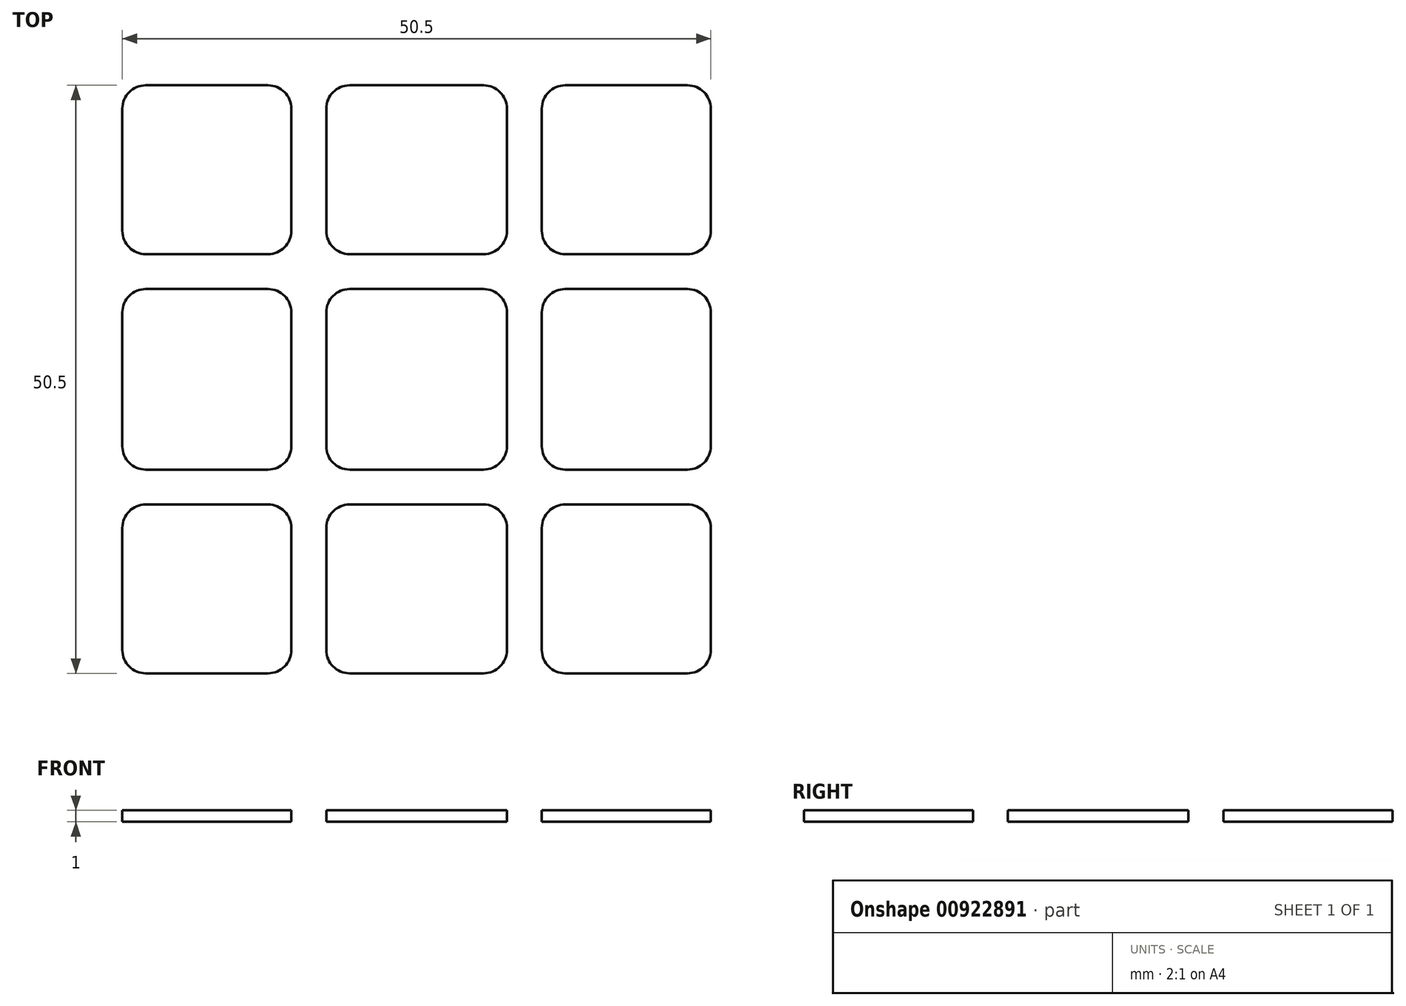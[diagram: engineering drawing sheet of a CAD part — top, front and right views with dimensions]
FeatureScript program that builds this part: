
annotation { "Feature Type Name" : "Feature", "Feature Type Description" : "" }
export const myFeature = defineFeature(function(context is Context, id is Id, definition is map)
    precondition{}
    {
        {
            var Q0;
            Q0=qCreatedBy(makeId("Top.planeOp"),FACE);
            var sketch = newSketch(context, id + "F0", { "sketchPlane" : qUnion([Q0])});
            skLineSegment(sketch, "E0.bottom", {"start": v(27.75, 27.75) * mm, "end": v(-27.75, 27.75) * mm, "construction": true});
            skLineSegment(sketch, "E0.top", {"start": v(27.75, -27.75) * mm, "end": v(-27.75, -27.75) * mm, "construction": true});
            skLineSegment(sketch, "E0.left", {"start": v(27.75, 27.75) * mm, "end": v(27.75, -27.75) * mm, "construction": true});
            skLineSegment(sketch, "E0.right", {"start": v(-27.75, 27.75) * mm, "end": v(-27.75, -27.75) * mm, "construction": true});
            skPoint(sketch, "E0.middle", {"position": v(0, 0) * mm});
            skLineSegment(sketch, "E1", {"start": v(-9.25, 27.75) * mm, "end": v(-9.25, -27.75) * mm, "construction": true});
            skLineSegment(sketch, "E2.1.0", {"start": v(-27.75, -9.25) * mm, "end": v(27.75, -9.25) * mm, "construction": true});
            skLineSegment(sketch, "E2.2.0", {"start": v(9.25, -27.75) * mm, "end": v(9.25, 27.75) * mm, "construction": true});
            skLineSegment(sketch, "E2.3.0", {"start": v(27.75, 9.25) * mm, "end": v(-27.75, 9.25) * mm, "construction": true});
            skLineSegment(sketch, "E3.bottom", {"start": v(-23.25, -10.75) * mm, "end": v(-12.75, -10.75) * mm});
            skLineSegment(sketch, "E3.top", {"start": v(-23.25, -25.25) * mm, "end": v(-12.75, -25.25) * mm});
            skLineSegment(sketch, "E3.left", {"start": v(-25.25, -12.75) * mm, "end": v(-25.25, -23.25) * mm});
            skLineSegment(sketch, "E3.right", {"start": v(-10.75, -12.75) * mm, "end": v(-10.75, -23.25) * mm});
            skLineSegment(sketch, "E4.bottom", {"start": v(-5.75, -10.75) * mm, "end": v(5.75, -10.75) * mm});
            skLineSegment(sketch, "E4.top", {"start": v(-5.75, -25.25) * mm, "end": v(5.75, -25.25) * mm});
            skLineSegment(sketch, "E4.left", {"start": v(-7.75, -12.75) * mm, "end": v(-7.75, -23.25) * mm});
            skLineSegment(sketch, "E4.right", {"start": v(7.75, -12.75) * mm, "end": v(7.75, -23.25) * mm});
            skLineSegment(sketch, "E5.bottom", {"start": v(5.75, 7.75) * mm, "end": v(-5.75, 7.75) * mm});
            skLineSegment(sketch, "E5.top", {"start": v(5.75, -7.75) * mm, "end": v(-5.75, -7.75) * mm});
            skLineSegment(sketch, "E5.left", {"start": v(7.75, 5.75) * mm, "end": v(7.75, -5.75) * mm});
            skLineSegment(sketch, "E5.right", {"start": v(-7.75, 5.75) * mm, "end": v(-7.75, -5.75) * mm});
            skPoint(sketch, "E6.visualSharp", {"position": v(-25.25, -10.75) * mm});
            skArc(sketch, "E6.filletArc", {"start": v(-23.25, -10.75) * mm, "mid": v(-24.66, -11.34) * mm, "end": v(-25.25, -12.75) * mm});
            skPoint(sketch, "E7.visualSharp", {"position": v(-25.25, -25.25) * mm});
            skArc(sketch, "E7.filletArc", {"start": v(-25.25, -23.25) * mm, "mid": v(-24.66, -24.66) * mm, "end": v(-23.25, -25.25) * mm});
            skPoint(sketch, "E8.visualSharp", {"position": v(-10.75, -25.25) * mm});
            skArc(sketch, "E8.filletArc", {"start": v(-12.75, -25.25) * mm, "mid": v(-11.34, -24.66) * mm, "end": v(-10.75, -23.25) * mm});
            skPoint(sketch, "E9.visualSharp", {"position": v(-10.75, -10.75) * mm});
            skArc(sketch, "E9.filletArc", {"start": v(-10.75, -12.75) * mm, "mid": v(-11.34, -11.34) * mm, "end": v(-12.75, -10.75) * mm});
            skPoint(sketch, "E10.visualSharp", {"position": v(-7.75, -10.75) * mm});
            skArc(sketch, "E10.filletArc", {"start": v(-5.75, -10.75) * mm, "mid": v(-7.16, -11.34) * mm, "end": v(-7.75, -12.75) * mm});
            skPoint(sketch, "E11.visualSharp", {"position": v(-7.75, -25.25) * mm});
            skArc(sketch, "E11.filletArc", {"start": v(-7.75, -23.25) * mm, "mid": v(-7.16, -24.66) * mm, "end": v(-5.75, -25.25) * mm});
            skPoint(sketch, "E12.visualSharp", {"position": v(7.75, -25.25) * mm});
            skArc(sketch, "E12.filletArc", {"start": v(5.75, -25.25) * mm, "mid": v(7.16, -24.66) * mm, "end": v(7.75, -23.25) * mm});
            skPoint(sketch, "E13.visualSharp", {"position": v(7.75, -10.75) * mm});
            skArc(sketch, "E13.filletArc", {"start": v(7.75, -12.75) * mm, "mid": v(7.16, -11.34) * mm, "end": v(5.75, -10.75) * mm});
            skPoint(sketch, "E14.visualSharp", {"position": v(7.75, -7.75) * mm});
            skArc(sketch, "E14.filletArc", {"start": v(5.75, -7.75) * mm, "mid": v(7.16, -7.16) * mm, "end": v(7.75, -5.75) * mm});
            skPoint(sketch, "E15.visualSharp", {"position": v(7.75, 7.75) * mm});
            skArc(sketch, "E15.filletArc", {"start": v(7.75, 5.75) * mm, "mid": v(7.16, 7.16) * mm, "end": v(5.75, 7.75) * mm});
            skPoint(sketch, "E16.visualSharp", {"position": v(-7.75, 7.75) * mm});
            skArc(sketch, "E16.filletArc", {"start": v(-5.75, 7.75) * mm, "mid": v(-7.16, 7.16) * mm, "end": v(-7.75, 5.75) * mm});
            skPoint(sketch, "E17.visualSharp", {"position": v(-7.75, -7.75) * mm});
            skArc(sketch, "E17.filletArc", {"start": v(-7.75, -5.75) * mm, "mid": v(-7.16, -7.16) * mm, "end": v(-5.75, -7.75) * mm});
            skLineSegment(sketch, "E18.1.0", {"start": v(10.75, -5.75) * mm, "end": v(10.75, 5.75) * mm});
            skPoint(sketch, "E18.1.1", {"position": v(10.75, -7.75) * mm});
            skPoint(sketch, "E18.1.2", {"position": v(25.25, -7.75) * mm});
            skLineSegment(sketch, "E18.1.3", {"start": v(25.25, -5.75) * mm, "end": v(25.25, 5.75) * mm});
            skPoint(sketch, "E18.1.4", {"position": v(10.75, -10.75) * mm});
            skLineSegment(sketch, "E18.1.5", {"start": v(12.75, -25.25) * mm, "end": v(23.25, -25.25) * mm});
            skLineSegment(sketch, "E18.1.6", {"start": v(12.75, -7.75) * mm, "end": v(23.25, -7.75) * mm});
            skPoint(sketch, "E18.1.7", {"position": v(25.25, -25.25) * mm});
            skLineSegment(sketch, "E18.1.8", {"start": v(12.75, -10.75) * mm, "end": v(23.25, -10.75) * mm});
            skLineSegment(sketch, "E18.1.9", {"start": v(10.75, -23.25) * mm, "end": v(10.75, -12.75) * mm});
            skLineSegment(sketch, "E18.1.10", {"start": v(12.75, 7.75) * mm, "end": v(23.25, 7.75) * mm});
            skLineSegment(sketch, "E18.1.11", {"start": v(25.25, -23.25) * mm, "end": v(25.25, -12.75) * mm});
            skPoint(sketch, "E18.1.12", {"position": v(25.25, 7.75) * mm});
            skPoint(sketch, "E18.1.13", {"position": v(10.75, 7.75) * mm});
            skPoint(sketch, "E18.1.14", {"position": v(25.25, -10.75) * mm});
            skPoint(sketch, "E18.1.15", {"position": v(10.75, -25.25) * mm});
            skArc(sketch, "E18.1.16", {"start": v(25.25, 5.75) * mm, "mid": v(24.66, 7.16) * mm, "end": v(23.25, 7.75) * mm});
            skArc(sketch, "E18.1.17", {"start": v(25.25, -12.75) * mm, "mid": v(24.66, -11.34) * mm, "end": v(23.25, -10.75) * mm});
            skArc(sketch, "E18.1.18", {"start": v(23.25, -7.75) * mm, "mid": v(24.66, -7.16) * mm, "end": v(25.25, -5.75) * mm});
            skArc(sketch, "E18.1.19", {"start": v(12.75, -10.75) * mm, "mid": v(11.34, -11.34) * mm, "end": v(10.75, -12.75) * mm});
            skArc(sketch, "E18.1.20", {"start": v(10.75, -23.25) * mm, "mid": v(11.34, -24.66) * mm, "end": v(12.75, -25.25) * mm});
            skArc(sketch, "E18.1.21", {"start": v(10.75, -5.75) * mm, "mid": v(11.34, -7.16) * mm, "end": v(12.75, -7.75) * mm});
            skArc(sketch, "E18.1.22", {"start": v(23.25, -25.25) * mm, "mid": v(24.66, -24.66) * mm, "end": v(25.25, -23.25) * mm});
            skArc(sketch, "E18.1.23", {"start": v(12.75, 7.75) * mm, "mid": v(11.34, 7.16) * mm, "end": v(10.75, 5.75) * mm});
            skLineSegment(sketch, "E18.2.0", {"start": v(5.75, 10.75) * mm, "end": v(-5.75, 10.75) * mm});
            skPoint(sketch, "E18.2.1", {"position": v(7.75, 10.75) * mm});
            skPoint(sketch, "E18.2.2", {"position": v(7.75, 25.25) * mm});
            skLineSegment(sketch, "E18.2.3", {"start": v(5.75, 25.25) * mm, "end": v(-5.75, 25.25) * mm});
            skPoint(sketch, "E18.2.4", {"position": v(10.75, 10.75) * mm});
            skLineSegment(sketch, "E18.2.5", {"start": v(25.25, 12.75) * mm, "end": v(25.25, 23.25) * mm});
            skLineSegment(sketch, "E18.2.6", {"start": v(7.75, 12.75) * mm, "end": v(7.75, 23.25) * mm});
            skPoint(sketch, "E18.2.7", {"position": v(25.25, 25.25) * mm});
            skLineSegment(sketch, "E18.2.8", {"start": v(10.75, 12.75) * mm, "end": v(10.75, 23.25) * mm});
            skLineSegment(sketch, "E18.2.9", {"start": v(23.25, 10.75) * mm, "end": v(12.75, 10.75) * mm});
            skLineSegment(sketch, "E18.2.10", {"start": v(-7.75, 12.75) * mm, "end": v(-7.75, 23.25) * mm});
            skLineSegment(sketch, "E18.2.11", {"start": v(23.25, 25.25) * mm, "end": v(12.75, 25.25) * mm});
            skPoint(sketch, "E18.2.12", {"position": v(-7.75, 25.25) * mm});
            skPoint(sketch, "E18.2.13", {"position": v(-7.75, 10.75) * mm});
            skPoint(sketch, "E18.2.14", {"position": v(10.75, 25.25) * mm});
            skPoint(sketch, "E18.2.15", {"position": v(25.25, 10.75) * mm});
            skArc(sketch, "E18.2.16", {"start": v(-5.75, 25.25) * mm, "mid": v(-7.16, 24.66) * mm, "end": v(-7.75, 23.25) * mm});
            skArc(sketch, "E18.2.17", {"start": v(12.75, 25.25) * mm, "mid": v(11.34, 24.66) * mm, "end": v(10.75, 23.25) * mm});
            skArc(sketch, "E18.2.18", {"start": v(7.75, 23.25) * mm, "mid": v(7.16, 24.66) * mm, "end": v(5.75, 25.25) * mm});
            skArc(sketch, "E18.2.19", {"start": v(10.75, 12.75) * mm, "mid": v(11.34, 11.34) * mm, "end": v(12.75, 10.75) * mm});
            skArc(sketch, "E18.2.20", {"start": v(23.25, 10.75) * mm, "mid": v(24.66, 11.34) * mm, "end": v(25.25, 12.75) * mm});
            skArc(sketch, "E18.2.21", {"start": v(5.75, 10.75) * mm, "mid": v(7.16, 11.34) * mm, "end": v(7.75, 12.75) * mm});
            skArc(sketch, "E18.2.22", {"start": v(25.25, 23.25) * mm, "mid": v(24.66, 24.66) * mm, "end": v(23.25, 25.25) * mm});
            skArc(sketch, "E18.2.23", {"start": v(-7.75, 12.75) * mm, "mid": v(-7.16, 11.34) * mm, "end": v(-5.75, 10.75) * mm});
            skLineSegment(sketch, "E18.3.0", {"start": v(-10.75, 5.75) * mm, "end": v(-10.75, -5.75) * mm});
            skPoint(sketch, "E18.3.1", {"position": v(-10.75, 7.75) * mm});
            skPoint(sketch, "E18.3.2", {"position": v(-25.25, 7.75) * mm});
            skLineSegment(sketch, "E18.3.3", {"start": v(-25.25, 5.75) * mm, "end": v(-25.25, -5.75) * mm});
            skPoint(sketch, "E18.3.4", {"position": v(-10.75, 10.75) * mm});
            skLineSegment(sketch, "E18.3.5", {"start": v(-12.75, 25.25) * mm, "end": v(-23.25, 25.25) * mm});
            skLineSegment(sketch, "E18.3.6", {"start": v(-12.75, 7.75) * mm, "end": v(-23.25, 7.75) * mm});
            skPoint(sketch, "E18.3.7", {"position": v(-25.25, 25.25) * mm});
            skLineSegment(sketch, "E18.3.8", {"start": v(-12.75, 10.75) * mm, "end": v(-23.25, 10.75) * mm});
            skLineSegment(sketch, "E18.3.9", {"start": v(-10.75, 23.25) * mm, "end": v(-10.75, 12.75) * mm});
            skLineSegment(sketch, "E18.3.10", {"start": v(-12.75, -7.75) * mm, "end": v(-23.25, -7.75) * mm});
            skLineSegment(sketch, "E18.3.11", {"start": v(-25.25, 23.25) * mm, "end": v(-25.25, 12.75) * mm});
            skPoint(sketch, "E18.3.12", {"position": v(-25.25, -7.75) * mm});
            skPoint(sketch, "E18.3.13", {"position": v(-10.75, -7.75) * mm});
            skPoint(sketch, "E18.3.14", {"position": v(-25.25, 10.75) * mm});
            skPoint(sketch, "E18.3.15", {"position": v(-10.75, 25.25) * mm});
            skArc(sketch, "E18.3.16", {"start": v(-25.25, -5.75) * mm, "mid": v(-24.66, -7.16) * mm, "end": v(-23.25, -7.75) * mm});
            skArc(sketch, "E18.3.17", {"start": v(-25.25, 12.75) * mm, "mid": v(-24.66, 11.34) * mm, "end": v(-23.25, 10.75) * mm});
            skArc(sketch, "E18.3.18", {"start": v(-23.25, 7.75) * mm, "mid": v(-24.66, 7.16) * mm, "end": v(-25.25, 5.75) * mm});
            skArc(sketch, "E18.3.19", {"start": v(-12.75, 10.75) * mm, "mid": v(-11.34, 11.34) * mm, "end": v(-10.75, 12.75) * mm});
            skArc(sketch, "E18.3.20", {"start": v(-10.75, 23.25) * mm, "mid": v(-11.34, 24.66) * mm, "end": v(-12.75, 25.25) * mm});
            skArc(sketch, "E18.3.21", {"start": v(-10.75, 5.75) * mm, "mid": v(-11.34, 7.16) * mm, "end": v(-12.75, 7.75) * mm});
            skArc(sketch, "E18.3.22", {"start": v(-23.25, 25.25) * mm, "mid": v(-24.66, 24.66) * mm, "end": v(-25.25, 23.25) * mm});
            skArc(sketch, "E18.3.23", {"start": v(-12.75, -7.75) * mm, "mid": v(-11.34, -7.16) * mm, "end": v(-10.75, -5.75) * mm});
            skSolve(sketch);
        }
        {
            var Q0;
            Q0 = qSketchRegion(id + "F0", true);
            var Q1;
            Q1 = qConstructionFilter(qBodyType(qCreatedBy(id + "F0" ,EDGE), BodyType.WIRE), ConstructionObject.NO);
            extrude(context, id + "F1", {"entities" : qUnion([Q0]), "surfaceEntities" : qUnion([Q1]), "depth" : 1 * mm, "offsetDistance" : 25 * mm});
        }
    });
